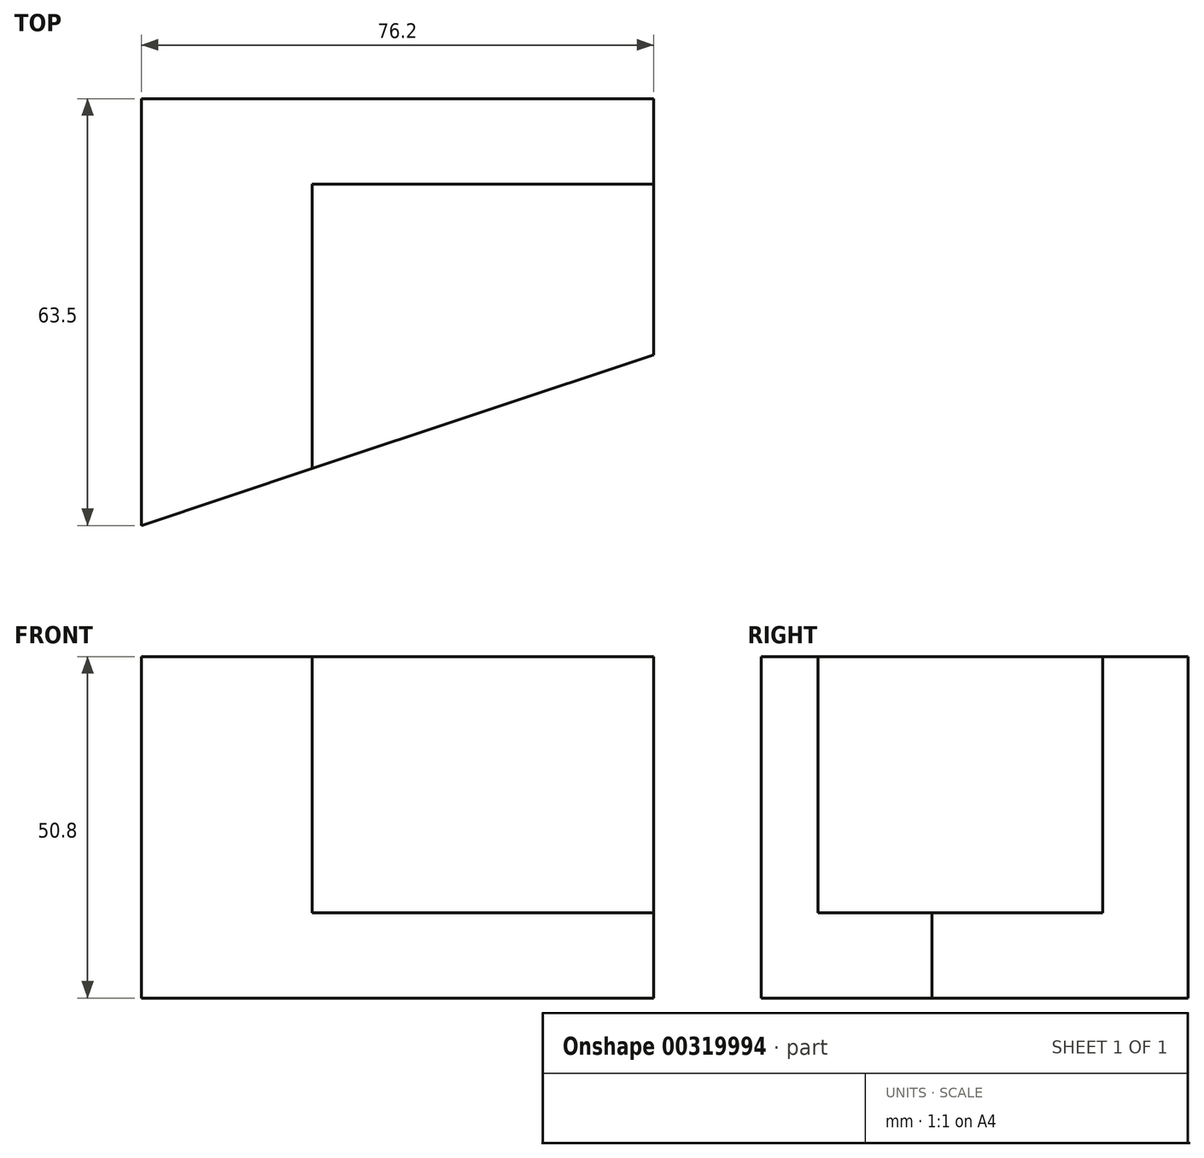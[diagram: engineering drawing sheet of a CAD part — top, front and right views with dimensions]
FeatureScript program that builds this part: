
annotation { "Feature Type Name" : "Feature", "Feature Type Description" : "" }
export const myFeature = defineFeature(function(context is Context, id is Id, definition is map)
    precondition{}
    {
        {
            var Q0;
            Q0=qCreatedBy(makeId("Top.planeOp"),FACE);
            var sketch = newSketch(context, id + "F0", { "sketchPlane" : qUnion([Q0])});
            skLineSegment(sketch, "E0.bottom", {"start": v(0, 0) * mm, "end": v(76.2, 0) * mm});
            skLineSegment(sketch, "E0.top", {"start": v(0, 63.5) * mm, "end": v(76.2, 63.5) * mm});
            skLineSegment(sketch, "E0.left", {"start": v(0, 0) * mm, "end": v(0, 63.5) * mm});
            skLineSegment(sketch, "E0.right", {"start": v(76.2, 0) * mm, "end": v(76.2, 63.5) * mm});
            skSolve(sketch);
        }
        {
            var Q0;
            Q0 = qSketchRegion(id + "F0", true);
            extrude(context, id + "F1", {"entities" : qUnion([Q0]), "depth" : 50.8 * mm});
        }
        {
            var Q0;
            Q0=makeQuery(id+"F1.opExtrude","CAP_FACE",FACE,{"disambiguationData":[OSD([sQuery(id+"F0.wireOp",EDGE,"E0.bottom"),sQuery(id+"F0.wireOp",EDGE,"E0.top"),sQuery(id+"F0.wireOp",EDGE,"E0.left"),sQuery(id+"F0.wireOp",EDGE,"E0.right")])],"isStart":false});
            var sketch = newSketch(context, id + "F2", { "sketchPlane" : qUnion([Q0])});
            skLineSegment(sketch, "E1", {"start": v(0, 0) * mm, "end": v(76.2, 25.4) * mm});
            skLineSegment(sketch, "E2", {"start": v(0, 0) * mm, "end": v(76.2, 0) * mm});
            skLineSegment(sketch, "E3", {"start": v(76.2, 0) * mm, "end": v(76.2, 25.4) * mm});
            skSolve(sketch);
        }
        {
            var Q0;
            Q0 = qSketchRegion(id + "F2", true);
            extrude(context, id + "F3", {"entities" : qUnion([Q0]), "operationType" : NewBodyOperationType.REMOVE, "oppositeDirection" : true, "depth" : 50.8 * mm});
        }
        {
            var Q0;
            Q0=makeQuery(id+"F1.opExtrude","CAP_FACE",FACE,{"disambiguationData":[OSD([sQuery(id+"F0.wireOp",EDGE,"E0.bottom"),sQuery(id+"F0.wireOp",EDGE,"E0.top"),sQuery(id+"F0.wireOp",EDGE,"E0.left"),sQuery(id+"F0.wireOp",EDGE,"E0.right")])],"isStart":false});
            var sketch = newSketch(context, id + "F4", { "sketchPlane" : qUnion([Q0])});
            skLineSegment(sketch, "E4", {"start": v(25.4, 8.47) * mm, "end": v(25.4, 50.8) * mm});
            skLineSegment(sketch, "E5", {"start": v(25.4, 50.8) * mm, "end": v(76.2, 50.8) * mm});
            skLineSegment(sketch, "E6", {"start": v(76.2, 50.8) * mm, "end": v(76.2, 25.4) * mm});
            skLineSegment(sketch, "E7", {"start": v(76.2, 25.4) * mm, "end": v(25.4, 8.47) * mm});
            skSolve(sketch);
        }
        {
            var Q0;
            Q0 = qSketchRegion(id + "F4", true);
            extrude(context, id + "F5", {"entities" : qUnion([Q0]), "operationType" : NewBodyOperationType.REMOVE, "oppositeDirection" : true, "depth" : 38.1 * mm});
        }
    });
